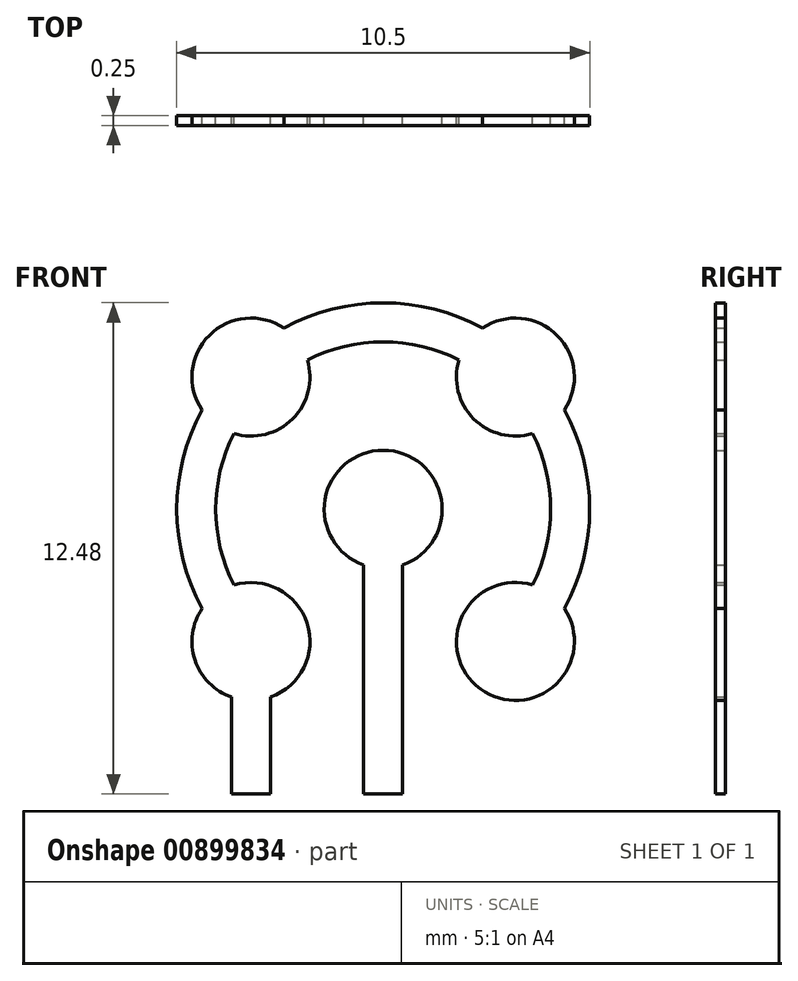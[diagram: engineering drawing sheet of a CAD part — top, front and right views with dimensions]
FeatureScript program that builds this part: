
annotation { "Feature Type Name" : "Feature", "Feature Type Description" : "" }
export const myFeature = defineFeature(function(context is Context, id is Id, definition is map)
    precondition{}
    {
        {
            var Q0;
            Q0=qCreatedBy(makeId("Front.planeOp"),FACE);
            var sketch = newSketch(context, id + "F0", { "sketchPlane" : qUnion([Q0])});
            skCircle(sketch, "E0", {"center": v(0, 0) * mm, "radius": 4.75 * mm, "construction": true});
            skLineSegment(sketch, "E1.bottom", {"start": v(-3.36, 3.36) * mm, "end": v(3.36, 3.36) * mm, "construction": true});
            skLineSegment(sketch, "E1.top", {"start": v(-3.36, -3.36) * mm, "end": v(3.36, -3.36) * mm, "construction": true});
            skLineSegment(sketch, "E1.left", {"start": v(-3.36, 3.36) * mm, "end": v(-3.36, -3.36) * mm, "construction": true});
            skLineSegment(sketch, "E1.right", {"start": v(3.36, 3.36) * mm, "end": v(3.36, -3.36) * mm, "construction": true});
            skArc(sketch, "E2", {"start": v(-3.8, 1.92) * mm, "mid": v(-2.3, 2.3) * mm, "end": v(-1.92, 3.8) * mm});
            skArc(sketch, "E3", {"start": v(1.92, 3.8) * mm, "mid": v(2.3, 2.3) * mm, "end": v(3.8, 1.92) * mm});
            skArc(sketch, "E4", {"start": v(-4.6, -2.52) * mm, "mid": v(-4.78, -3.83) * mm, "end": v(-3.85, -4.77) * mm});
            skArc(sketch, "E5", {"start": v(3.8, -1.92) * mm, "mid": v(2.47, -4.56) * mm, "end": v(4.6, -2.52) * mm});
            skArc(sketch, "E6.0", {"start": v(4.6, -2.52) * mm, "mid": v(5.25, 0) * mm, "end": v(4.6, 2.52) * mm});
            skArc(sketch, "E7", {"start": v(0.5, -1.41) * mm, "mid": v(0, 1.5) * mm, "end": v(-0.5, -1.41) * mm});
            skArc(sketch, "E8.0", {"start": v(3.8, -1.92) * mm, "mid": v(4.25, 0) * mm, "end": v(3.8, 1.92) * mm});
            skLineSegment(sketch, "E9.top", {"start": v(-0.5, -7.23) * mm, "end": v(0.5, -7.23) * mm});
            skLineSegment(sketch, "E9.left", {"start": v(-0.5, -1.41) * mm, "end": v(-0.5, -7.23) * mm});
            skLineSegment(sketch, "E9.right", {"start": v(0.5, -1.41) * mm, "end": v(0.5, -7.23) * mm});
            skPoint(sketch, "E10.orphan", {"position": v(0.5, 0) * mm});
            skPoint(sketch, "E9.bottom.start.orphan", {"position": v(-0.5, 0) * mm});
            skArc(sketch, "E11.trimOffspring", {"start": v(-4.6, 2.52) * mm, "mid": v(-5.25, 0) * mm, "end": v(-4.6, -2.52) * mm});
            skArc(sketch, "E12.trimOffspring", {"start": v(2.52, 4.6) * mm, "mid": v(0, 5.25) * mm, "end": v(-2.52, 4.6) * mm});
            skArc(sketch, "E13.trimOffspring", {"start": v(-2.52, 4.6) * mm, "mid": v(-4.42, 4.42) * mm, "end": v(-4.6, 2.52) * mm});
            skArc(sketch, "E14.trimOffspring", {"start": v(4.6, 2.52) * mm, "mid": v(4.42, 4.42) * mm, "end": v(2.52, 4.6) * mm});
            skArc(sketch, "E15.trimOffspring", {"start": v(1.92, 3.8) * mm, "mid": v(0, 4.25) * mm, "end": v(-1.92, 3.8) * mm});
            skArc(sketch, "E16.trimOffspring", {"start": v(-3.8, 1.92) * mm, "mid": v(-4.25, 0) * mm, "end": v(-3.8, -1.92) * mm});
            skLineSegment(sketch, "E17", {"start": v(-3.85, -4.77) * mm, "end": v(-3.85, -7.23) * mm});
            skLineSegment(sketch, "E18", {"start": v(-3.85, -7.23) * mm, "end": v(-2.86, -7.23) * mm});
            skLineSegment(sketch, "E19", {"start": v(-2.86, -7.23) * mm, "end": v(-2.86, -4.77) * mm});
            skLineSegment(sketch, "E20", {"start": v(-3.36, -7.23) * mm, "end": v(-3.36, -3.36) * mm, "construction": true});
            skArc(sketch, "E21.trimOffspring", {"start": v(-2.86, -4.77) * mm, "mid": v(-1.93, -2.9) * mm, "end": v(-3.8, -1.92) * mm});
            skSolve(sketch);
        }
        {
            var Q0;
            Q0=makeQuery(id+"F0.imprint","IMPRINT",FACE,{"disambiguationData":[TD([[makeQuery(id+"F0.imprint","IMPRINT",EDGE,{"derivedFrom":sQuery(id+"F0.wireOp",EDGE,"E2")}),1.0]])]});
            var Q1;
            Q1=makeQuery(id+"F0.imprint","IMPRINT",FACE,{"disambiguationData":[TD([[makeQuery(id+"F0.imprint","IMPRINT",EDGE,{"derivedFrom":sQuery(id+"F0.wireOp",EDGE,"E7")}),1.0]])]});
            extrude(context, id + "F1", {"entities" : qUnion([Q0, Q1]), "depth" : 0.25 * mm, "offsetDistance" : 25.4 * mm});
        }
    });
